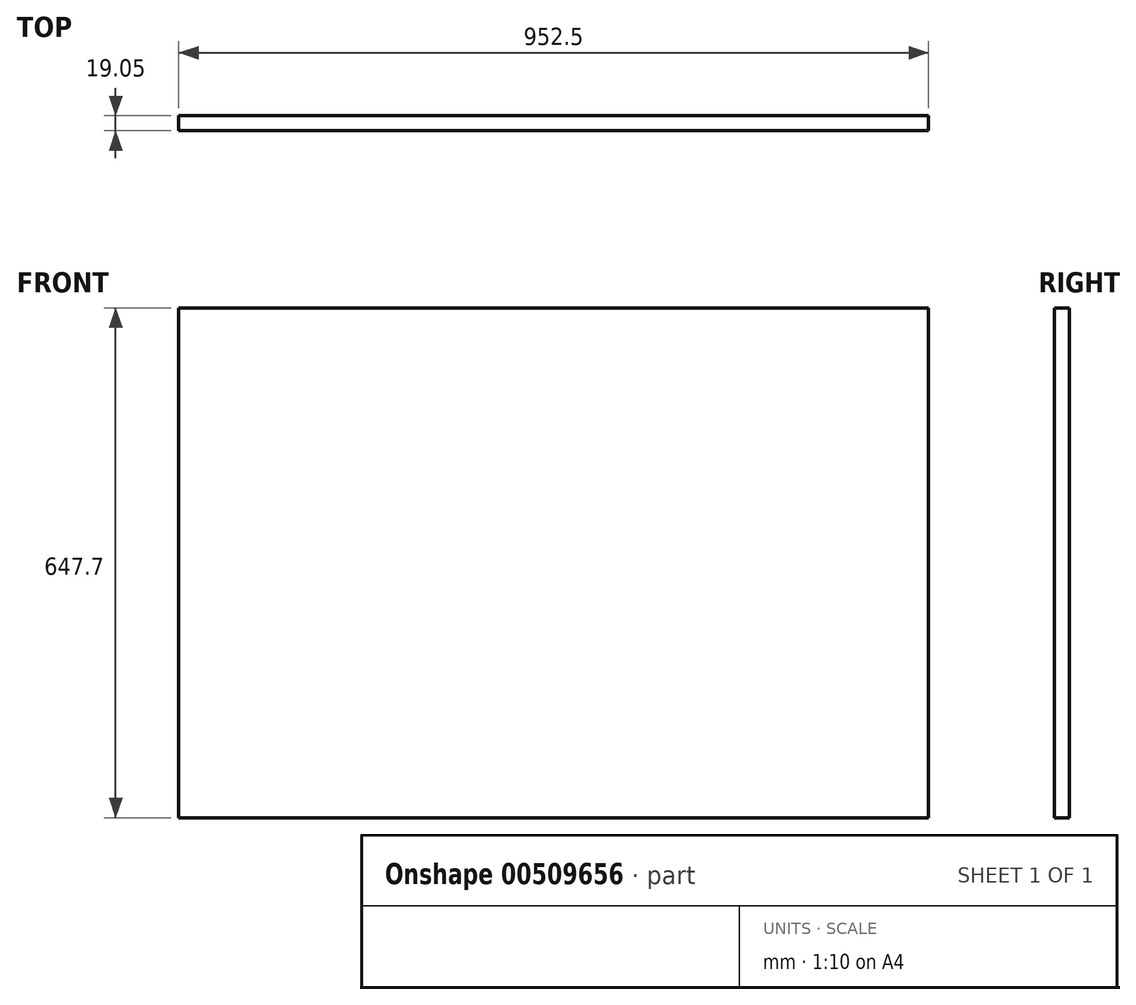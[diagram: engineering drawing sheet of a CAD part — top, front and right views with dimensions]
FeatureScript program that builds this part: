
annotation { "Feature Type Name" : "Feature", "Feature Type Description" : "" }
export const myFeature = defineFeature(function(context is Context, id is Id, definition is map)
    precondition{}
    {
        {
            var Q0;
            Q0=qCreatedBy(makeId("Front.planeOp"),FACE);
            var sketch = newSketch(context, id + "F0", { "sketchPlane" : qUnion([Q0])});
            skLineSegment(sketch, "E0.bottom", {"start": v(-474.7, 454.74) * mm, "end": v(477.8, 454.74) * mm});
            skLineSegment(sketch, "E0.top", {"start": v(-474.7, -192.96) * mm, "end": v(477.8, -192.96) * mm});
            skLineSegment(sketch, "E0.left", {"start": v(-474.7, 454.74) * mm, "end": v(-474.7, -192.96) * mm});
            skLineSegment(sketch, "E0.right", {"start": v(477.8, 454.74) * mm, "end": v(477.8, -192.96) * mm});
            skSolve(sketch);
        }
        {
            var Q0;
            Q0=qSketchRegion(id+"F0",true);
            extrude(context, id + "F1", {"entities" : qUnion([Q0]), "depth" : 19.05 * mm});
        }
    });
